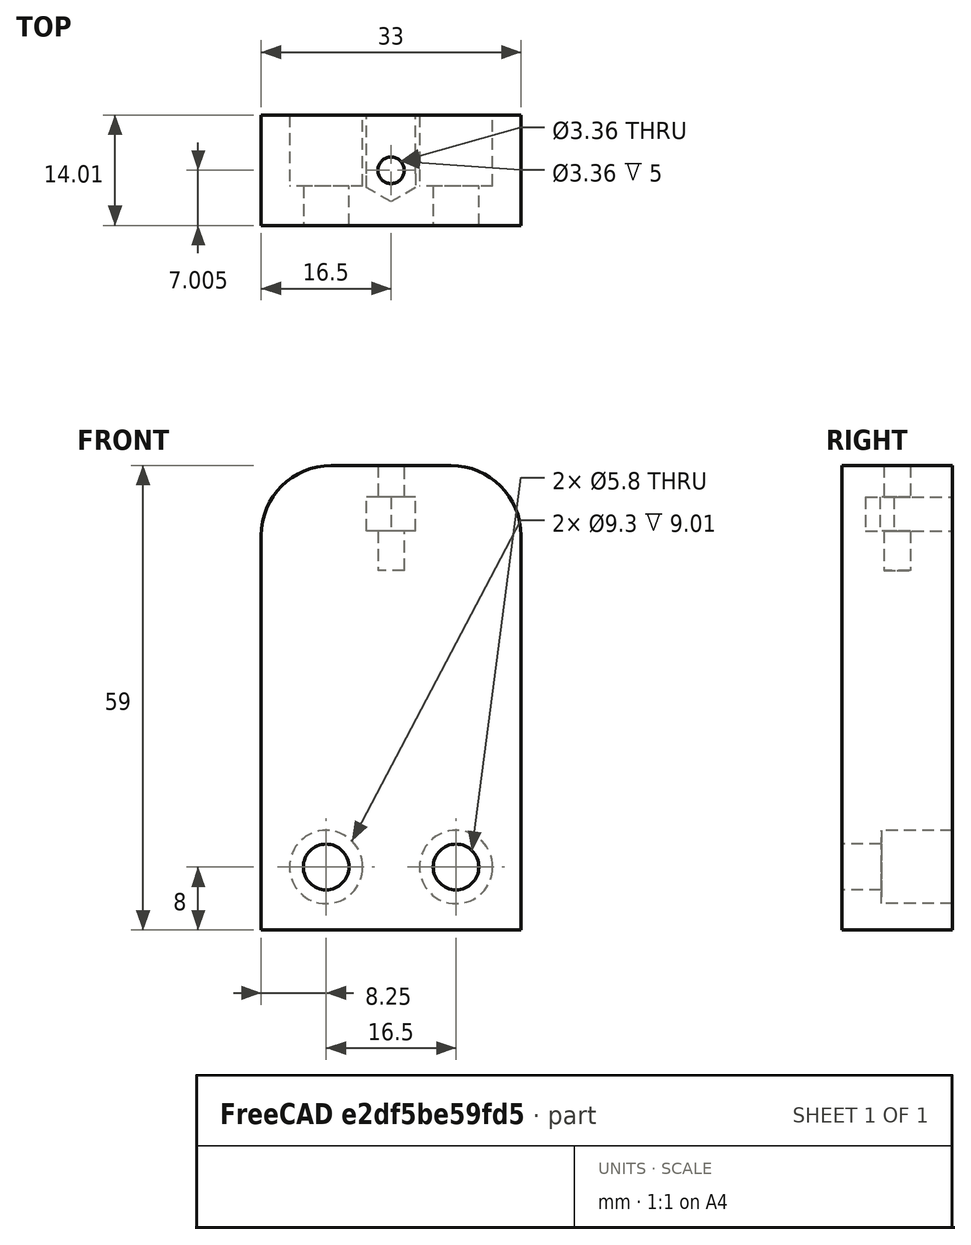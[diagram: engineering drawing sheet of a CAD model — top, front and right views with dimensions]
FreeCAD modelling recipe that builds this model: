
FCSTD DOCUMENT  (FreeCAD 0.16R6706 (Git))
Label: idler_pulley_holder_41_above_h
License: All rights reserved
LicenseURL: http://en.wikipedia.org/wiki/All_rights_reserved
objects: Part::Feature×1, Part::Fillet×1, Part::Prism×1, Part::Box×1, Part::Fuse×1, Part::Cut×1
note: 6 computed .brp shape members not serialized (recipe doc carries the construction recipe); baked Part::Feature solids carry a one-line shape summary decoded from their .brp

FEATURE [Part::Feature] idlepulleyhold_aux
  shape: bbox 33 x 14.01 x 59 mm, 14 faces (baked)
FEATURE [Part::Fillet] idlepulleyhold_chmf
  Base = -> idlepulleyhold_aux
  Edges = 2 edges r=8.895: [Edge9,Edge12]
FEATURE [Part::Prism] idlepulleyhold_nuthole_nut
  Circumradius = 3.605
  Height = 4.32
  Placement = pos=(0,0,0) rot=(-0.57735,0.57735,0.57735;2.0944rad)
  Polygon = 6
FEATURE [Part::Box] idlepulleyhold_nuthole_hole
  Height = 8.405
  Length = 6.24408
  Placement = pos=(-3.12204,0,0) rot=(0,0,1;0rad)
  Width = 4.32
FEATURE [Part::Fuse] idlepulleyhold_nuthole
  Base = -> idlepulleyhold_nuthole_nut
  Placement = pos=(0,6.605,37) rot=(-1,0,0;1.5708rad)
  Tool = -> idlepulleyhold_nuthole_hole
FEATURE [Part::Cut] idlepulleyhold
  Base = -> idlepulleyhold_chmf
  Tool = -> idlepulleyhold_nuthole
